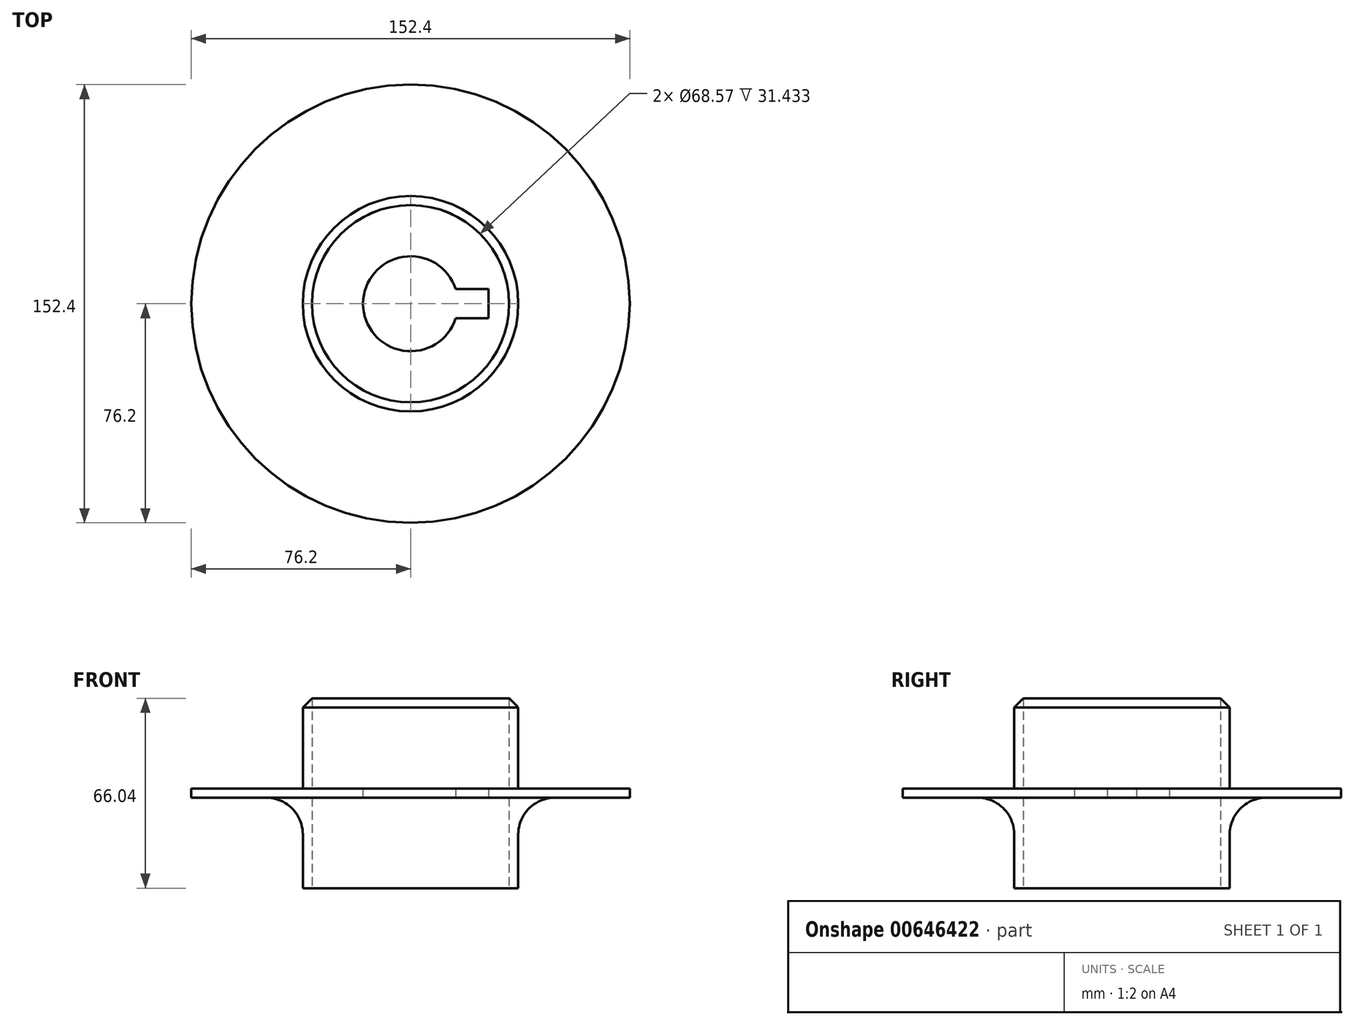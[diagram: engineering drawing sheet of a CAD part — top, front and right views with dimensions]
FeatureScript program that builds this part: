
annotation { "Feature Type Name" : "Feature", "Feature Type Description" : "" }
export const myFeature = defineFeature(function(context is Context, id is Id, definition is map)
    precondition{}
    {
        {
            var Q0;
            Q0=qCreatedBy(makeId("Top.planeOp"),FACE);
            var sketch = newSketch(context, id + "F0", { "sketchPlane" : qUnion([Q0])});
            skCircle(sketch, "E0", {"center": v(0, 0) * mm, "radius": 37.47 * mm});
            skCircle(sketch, "E1.0", {"center": v(0, 0) * mm, "radius": 34.28 * mm});
            skSolve(sketch);
        }
        {
            var Q0;
            Q0 = qSketchRegion(id + "F0", true);
            extrude(context, id + "F1", {"entities" : qUnion([Q0]), "depth" : 33.02 * mm, "offsetDistance" : 25.4 * mm, "hasSecondDirection" : true, "secondDirectionOppositeDirection" : true, "secondDirectionDepth" : 33.02 * mm});
        }
        {
            var Q0;
            Q0=makeQuery(id+"F1.opExtrude","CAP_EDGE",EDGE,{"disambiguationData":[OSD([sQuery(id+"F0.wireOp",EDGE,"E0")])],"isStart":false});
            chamfer(context, id + "F2", {"entities" : qUnion([Q0]), "width" : 3.17 * mm, "tangentPropagation" : true});
        }
        {
            var Q0;
            Q0=qCreatedBy(makeId("Top.planeOp"),FACE);
            var sketch = newSketch(context, id + "F3", { "sketchPlane" : qUnion([Q0])});
            skArc(sketch, "E2", {"start": v(15.7, 5.08) * mm, "mid": v(-16.51, 0) * mm, "end": v(15.7, -5.08) * mm});
            skCircle(sketch, "E3", {"center": v(0, 0) * mm, "radius": 76.2 * mm});
            skLineSegment(sketch, "E4.bottom", {"start": v(15.7, 5.08) * mm, "end": v(27.08, 5.08) * mm});
            skLineSegment(sketch, "E4.top", {"start": v(15.7, -5.08) * mm, "end": v(27.08, -5.08) * mm});
            skLineSegment(sketch, "E4.right", {"start": v(27.08, 5.08) * mm, "end": v(27.08, -5.08) * mm});
            skPoint(sketch, "E4.middle", {"position": v(16.51, 0) * mm});
            skPoint(sketch, "E5.orphan", {"position": v(5.94, 5.08) * mm});
            skPoint(sketch, "E6.orphan", {"position": v(5.94, -5.08) * mm});
            skSolve(sketch);
        }
        {
            var Q0;
            Q0 = qSketchRegion(id + "F3", true);
            extrude(context, id + "F4", {"entities" : qUnion([Q0]), "operationType" : NewBodyOperationType.ADD, "depth" : 1.59 * mm, "offsetDistance" : 25.4 * mm, "hasSecondDirection" : true, "secondDirectionOppositeDirection" : true, "secondDirectionDepth" : 1.59 * mm});
        }
        {
            var Q0;
            Q0=makeQuery(id+"F4.boolean.opBoolean","INTERSECT",EDGE,{"derivedFrom":[makeQuery(id+"F1.opExtrude","SWEPT_FACE",FACE,{"disambiguationData":[OSD([sQuery(id+"F0.wireOp",EDGE,"E0")])]}),makeQuery(id+"F4.opExtrude","CAP_FACE",FACE,{"disambiguationData":[OSD([sQuery(id+"F3.wireOp",EDGE,"E2"),sQuery(id+"F3.wireOp",EDGE,"E3"),sQuery(id+"F3.wireOp",EDGE,"E4.bottom"),sQuery(id+"F3.wireOp",EDGE,"E4.top"),sQuery(id+"F3.wireOp",EDGE,"E4.right")])],"isStart":true})]});
            fillet(context, id + "F5", {"entities" : qUnion([Q0]), "radius" : 12.7 * mm, "tangentPropagation" : true, "allowEdgeOverflow" : false});
        }
    });
